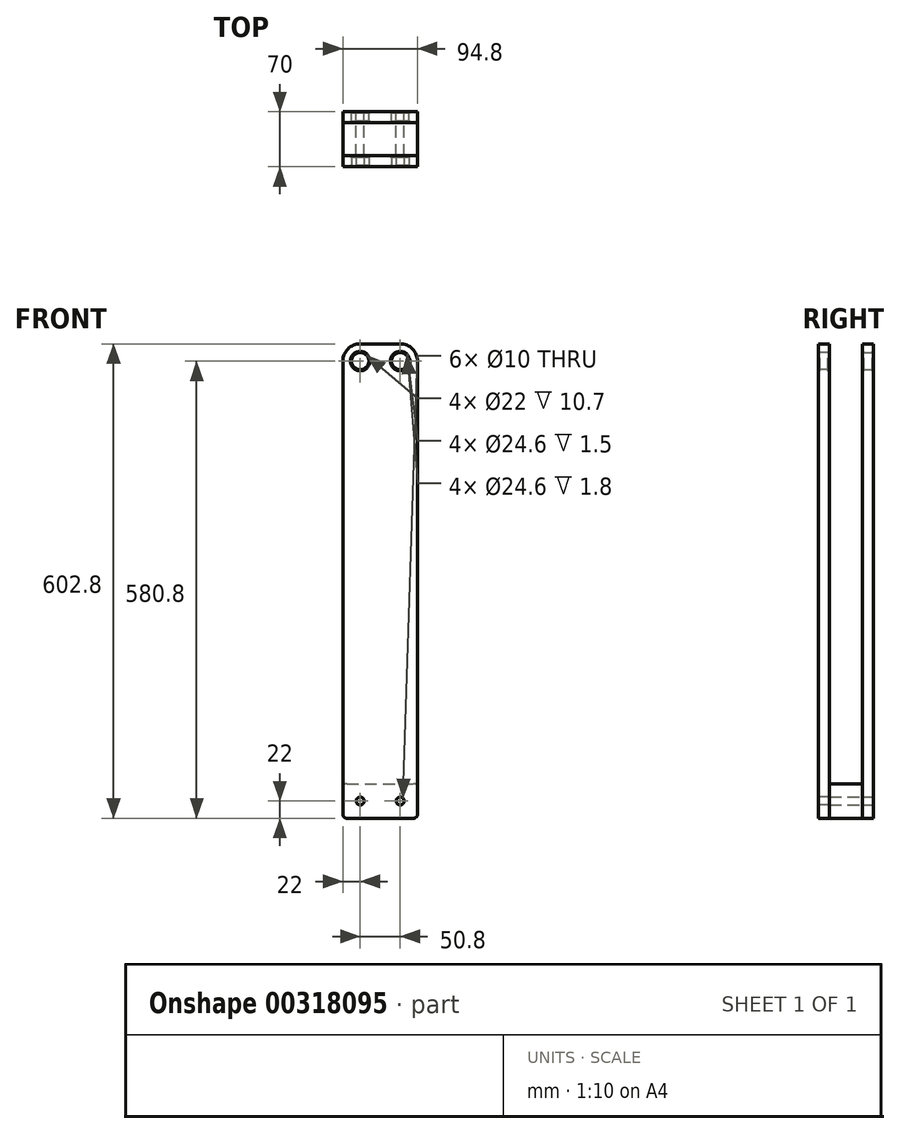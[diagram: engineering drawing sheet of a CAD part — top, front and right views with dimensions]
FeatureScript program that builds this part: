
annotation { "Feature Type Name" : "Feature", "Feature Type Description" : "" }
export const myFeature = defineFeature(function(context is Context, id is Id, definition is map)
    precondition{}
    {
        {
            var Q0;
            Q0=qCreatedBy(makeId("Front.planeOp"),FACE);
            var sketch = newSketch(context, id + "F0", { "sketchPlane" : qUnion([Q0])});
            skLineSegment(sketch, "E0.bottom", {"start": v(25.4, 279.4) * mm, "end": v(-25.4, 279.4) * mm, "construction": true});
            skLineSegment(sketch, "E0.top", {"start": v(25.4, -279.4) * mm, "end": v(-25.4, -279.4) * mm, "construction": true});
            skLineSegment(sketch, "E0.left", {"start": v(25.4, 279.4) * mm, "end": v(25.4, -279.4) * mm, "construction": true});
            skLineSegment(sketch, "E0.right", {"start": v(-25.4, 279.4) * mm, "end": v(-25.4, -279.4) * mm, "construction": true});
            skPoint(sketch, "E0.middle", {"position": v(0, 0) * mm});
            skPoint(sketch, "E1", {"position": v(0, 279.4) * mm});
            skCircle(sketch, "E2", {"center": v(-25.4, 279.4) * mm, "radius": 11 * mm});
            skCircle(sketch, "E3", {"center": v(25.4, 279.4) * mm, "radius": 11 * mm});
            skLineSegment(sketch, "E4.bottom", {"start": v(-25.4, 301.4) * mm, "end": v(25.4, 301.4) * mm});
            skLineSegment(sketch, "E4.top", {"start": v(-42.4, -301.4) * mm, "end": v(42.4, -301.4) * mm});
            skLineSegment(sketch, "E4.left", {"start": v(-47.4, 279.4) * mm, "end": v(-47.4, -296.4) * mm});
            skLineSegment(sketch, "E4.right", {"start": v(47.4, 279.4) * mm, "end": v(47.4, -296.4) * mm});
            skPoint(sketch, "E5.orphan", {"position": v(-47.4, 301.4) * mm});
            skPoint(sketch, "E6.orphan", {"position": v(47.4, 301.4) * mm});
            skPoint(sketch, "E7.visualSharp", {"position": v(-47.4, -301.4) * mm});
            skArc(sketch, "E7.filletArc", {"start": v(-47.4, -296.4) * mm, "mid": v(-45.94, -299.94) * mm, "end": v(-42.4, -301.4) * mm});
            skPoint(sketch, "E8.visualSharp", {"position": v(47.4, -301.4) * mm});
            skArc(sketch, "E8.filletArc", {"start": v(42.4, -301.4) * mm, "mid": v(45.94, -299.94) * mm, "end": v(47.4, -296.4) * mm});
            skCircle(sketch, "E9", {"center": v(-25.4, 279.4) * mm, "radius": 12.3 * mm});
            skCircle(sketch, "E10", {"center": v(25.4, 279.4) * mm, "radius": 12.3 * mm});
            skArc(sketch, "E11", {"start": v(-25.4, 301.4) * mm, "mid": v(-40.96, 294.96) * mm, "end": v(-47.4, 279.4) * mm});
            skArc(sketch, "E12", {"start": v(47.4, 279.4) * mm, "mid": v(40.96, 294.96) * mm, "end": v(25.4, 301.4) * mm});
            skCircle(sketch, "E13", {"center": v(-25.4, -279.4) * mm, "radius": 5 * mm});
            skCircle(sketch, "E14", {"center": v(25.4, -279.4) * mm, "radius": 5 * mm});
            skSolve(sketch);
        }
        {
            var Q0;
            Q0 = qSketchRegion(id + "F0", true);
            var Q1;
            Q1=makeQuery(id+"F0.imprint","IMPRINT",FACE,{"disambiguationData":[TD([[makeQuery(id+"F0.imprint","IMPRINT",EDGE,{"derivedFrom":sQuery(id+"F0.wireOp",EDGE,"E2")}),-1.0]])]});
            var Q2;
            Q2=makeQuery(id+"F0.imprint","IMPRINT",FACE,{"disambiguationData":[TD([[makeQuery(id+"F0.imprint","IMPRINT",EDGE,{"derivedFrom":sQuery(id+"F0.wireOp",EDGE,"E3")}),-1.0]])]});
            extrude(context, id + "F1", {"entities" : qUnion([Q0, Q1, Q2]), "depth" : 14 * mm});
        }
        {
            var Q0;
            Q0=makeQuery(id+"F0.imprint","IMPRINT",FACE,{"disambiguationData":[TD([[makeQuery(id+"F0.imprint","IMPRINT",EDGE,{"derivedFrom":sQuery(id+"F0.wireOp",EDGE,"E2")}),-1.0]])]});
            var Q1;
            Q1=makeQuery(id+"F0.imprint","IMPRINT",FACE,{"disambiguationData":[TD([[makeQuery(id+"F0.imprint","IMPRINT",EDGE,{"derivedFrom":sQuery(id+"F0.wireOp",EDGE,"E3")}),-1.0]])]});
            extrude(context, id + "F2", {"entities" : qUnion([Q0, Q1]), "operationType" : NewBodyOperationType.REMOVE, "depth" : 1.5 * mm});
        }
        {
            var Q0;
            Q0=makeQuery(id+"F1.opExtrude","CAP_FACE",FACE,{"disambiguationData":[OSD([sQuery(id+"F0.wireOp",EDGE,"E2"),sQuery(id+"F0.wireOp",EDGE,"E3"),sQuery(id+"F0.wireOp",EDGE,"E4.bottom"),sQuery(id+"F0.wireOp",EDGE,"E4.top"),sQuery(id+"F0.wireOp",EDGE,"E4.left"),sQuery(id+"F0.wireOp",EDGE,"E4.right"),sQuery(id+"F0.wireOp",EDGE,"E7.filletArc"),sQuery(id+"F0.wireOp",EDGE,"E8.filletArc"),sQuery(id+"F0.wireOp",EDGE,"E11"),sQuery(id+"F0.wireOp",EDGE,"E12")])],"isStart":false});
            var sketch = newSketch(context, id + "F3", { "sketchPlane" : qUnion([Q0])});
            skCircle(sketch, "E15.0", {"center": v(-25.4, 279.4) * mm, "radius": 12.3 * mm});
            skCircle(sketch, "E16.0", {"center": v(25.4, 279.4) * mm, "radius": 12.3 * mm});
            skCircle(sketch, "E17.0", {"center": v(25.4, 279.4) * mm, "radius": 11 * mm});
            skCircle(sketch, "E18.0", {"center": v(-25.4, 279.4) * mm, "radius": 11 * mm});
            skSolve(sketch);
        }
        {
            var Q0;
            Q0 = qSketchRegion(id + "F3", true);
            extrude(context, id + "F4", {"entities" : qUnion([Q0]), "operationType" : NewBodyOperationType.REMOVE, "oppositeDirection" : true, "depth" : 1.8 * mm});
        }
        {
            var Q0;
            Q0=makeQuery(id+"F1.opExtrude","CAP_FACE",FACE,{"disambiguationData":[OSD([sQuery(id+"F0.wireOp",EDGE,"E2"),sQuery(id+"F0.wireOp",EDGE,"E3"),sQuery(id+"F0.wireOp",EDGE,"E4.bottom"),sQuery(id+"F0.wireOp",EDGE,"E4.top"),sQuery(id+"F0.wireOp",EDGE,"E4.left"),sQuery(id+"F0.wireOp",EDGE,"E4.right"),sQuery(id+"F0.wireOp",EDGE,"E7.filletArc"),sQuery(id+"F0.wireOp",EDGE,"E8.filletArc"),sQuery(id+"F0.wireOp",EDGE,"E11"),sQuery(id+"F0.wireOp",EDGE,"E12"),sQuery(id+"F0.wireOp",EDGE,"E13"),sQuery(id+"F0.wireOp",EDGE,"E14")])],"isStart":false});
            var sketch = newSketch(context, id + "F5", { "sketchPlane" : qUnion([Q0])});
            skLineSegment(sketch, "E19.0", {"start": v(-47.4, -262.4) * mm, "end": v(-47.4, -296.4) * mm});
            skPoint(sketch, "E20.0", {"position": v(-45.94, -299.94) * mm});
            skArc(sketch, "E21.0", {"start": v(-47.4, -296.4) * mm, "mid": v(-45.94, -299.94) * mm, "end": v(-42.4, -301.4) * mm});
            skLineSegment(sketch, "E22.0", {"start": v(-42.4, -301.4) * mm, "end": v(42.4, -301.4) * mm});
            skArc(sketch, "E23.0", {"start": v(42.4, -301.4) * mm, "mid": v(45.94, -299.94) * mm, "end": v(47.4, -296.4) * mm});
            skLineSegment(sketch, "E24.0", {"start": v(47.4, -262.4) * mm, "end": v(47.4, -296.4) * mm});
            skArc(sketch, "E25.MirrorCS", {"start": v(-47.4, -262.4) * mm, "mid": v(-45.94, -258.86) * mm, "end": v(-42.4, -257.4) * mm});
            skLineSegment(sketch, "E26.MirrorCS", {"start": v(-42.4, -257.4) * mm, "end": v(42.4, -257.4) * mm});
            skArc(sketch, "E27.MirrorCS", {"start": v(42.4, -257.4) * mm, "mid": v(45.94, -258.86) * mm, "end": v(47.4, -262.4) * mm});
            skPoint(sketch, "E28.MirrorP", {"position": v(-45.94, -258.86) * mm});
            skPoint(sketch, "E29.orphan", {"position": v(47.4, 279.4) * mm});
            skPoint(sketch, "E30.orphan", {"position": v(-47.4, 279.4) * mm});
            skCircle(sketch, "E31.0", {"center": v(-25.4, -279.4) * mm, "radius": 5 * mm});
            skCircle(sketch, "E32.0", {"center": v(25.4, -279.4) * mm, "radius": 5 * mm});
            skSolve(sketch);
        }
        {
            var Q0;
            Q0 = qSketchRegion(id + "F5", true);
            extrude(context, id + "F6", {"entities" : qUnion([Q0]), "depth" : (14 + 14 + 14) * mm});
        }
        {
            var Q0;
            Q0=makeQuery(id+"F1.opExtrude","CAP_FACE",FACE,{"disambiguationData":[OSD([sQuery(id+"F0.wireOp",EDGE,"E2"),sQuery(id+"F0.wireOp",EDGE,"E3"),sQuery(id+"F0.wireOp",EDGE,"E4.bottom"),sQuery(id+"F0.wireOp",EDGE,"E4.top"),sQuery(id+"F0.wireOp",EDGE,"E4.left"),sQuery(id+"F0.wireOp",EDGE,"E4.right"),sQuery(id+"F0.wireOp",EDGE,"E7.filletArc"),sQuery(id+"F0.wireOp",EDGE,"E8.filletArc"),sQuery(id+"F0.wireOp",EDGE,"E11"),sQuery(id+"F0.wireOp",EDGE,"E12"),sQuery(id+"F0.wireOp",EDGE,"E13"),sQuery(id+"F0.wireOp",EDGE,"E14")])],"isStart":false});
            cPlane(context, id + "F7", {"entities" : qUnion([Q0]), "cplaneType" : CPlaneType.OFFSET, "offset" : (14 + 7) * mm, "width" : 150 * mm, "height" : 150 * mm});
        }
        {
            var Q0;
            Q0=makeQuery(id+"F1.opExtrude","SWEPT_BODY",BODY,{"disambiguationData":[OSD([sQuery(id+"F0.wireOp",EDGE,"E2"),sQuery(id+"F0.wireOp",EDGE,"E3"),sQuery(id+"F0.wireOp",EDGE,"E4.bottom"),sQuery(id+"F0.wireOp",EDGE,"E4.top"),sQuery(id+"F0.wireOp",EDGE,"E4.left"),sQuery(id+"F0.wireOp",EDGE,"E4.right"),sQuery(id+"F0.wireOp",EDGE,"E7.filletArc"),sQuery(id+"F0.wireOp",EDGE,"E8.filletArc"),sQuery(id+"F0.wireOp",EDGE,"E11"),sQuery(id+"F0.wireOp",EDGE,"E12"),sQuery(id+"F0.wireOp",EDGE,"E13"),sQuery(id+"F0.wireOp",EDGE,"E14")])]});
            var Q1;
            Q1=qCreatedBy(id+"F7.planeOp",FACE);
            mirror(context, id + "F8", {"entities" : qUnion([Q0]), "mirrorPlane" : qUnion([Q1])});
        }
    });
